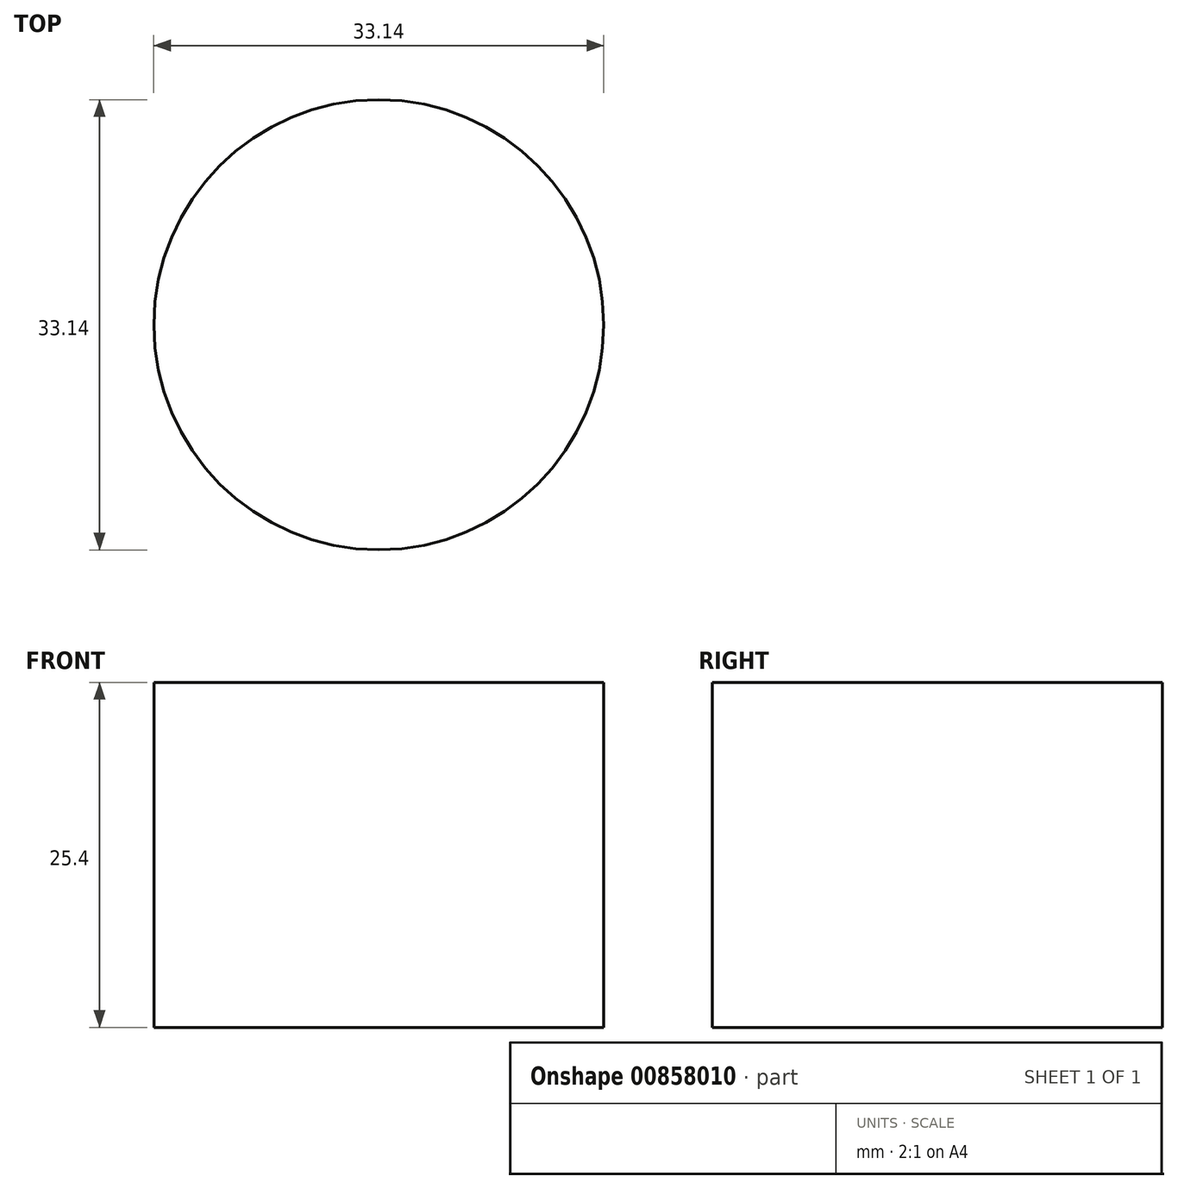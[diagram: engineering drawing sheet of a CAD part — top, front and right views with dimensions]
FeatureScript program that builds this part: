
annotation { "Feature Type Name" : "Feature", "Feature Type Description" : "" }
export const myFeature = defineFeature(function(context is Context, id is Id, definition is map)
    precondition{}
    {
        {
            var Q0;
            Q0=qCreatedBy(makeId("Top.planeOp"),FACE);
            var sketch = newSketch(context, id + "F0", { "sketchPlane" : qUnion([Q0])});
            skCircle(sketch, "E0", {"center": v(0, 0) * mm, "radius": 16.57 * mm});
            skSolve(sketch);
        }
        {
            var Q0;
            Q0=makeQuery(id+"F0.imprint","IMPRINT",FACE,{"disambiguationData":[TD([[makeQuery(id+"F0.imprint","IMPRINT",EDGE,{"derivedFrom":sQuery(id+"F0.wireOp",EDGE,"E0")}),1.0]])]});
            extrude(context, id + "F1", {"entities" : qUnion([Q0]), "depth" : 25.4 * mm, "offsetDistance" : 25.4 * mm});
        }
    });
